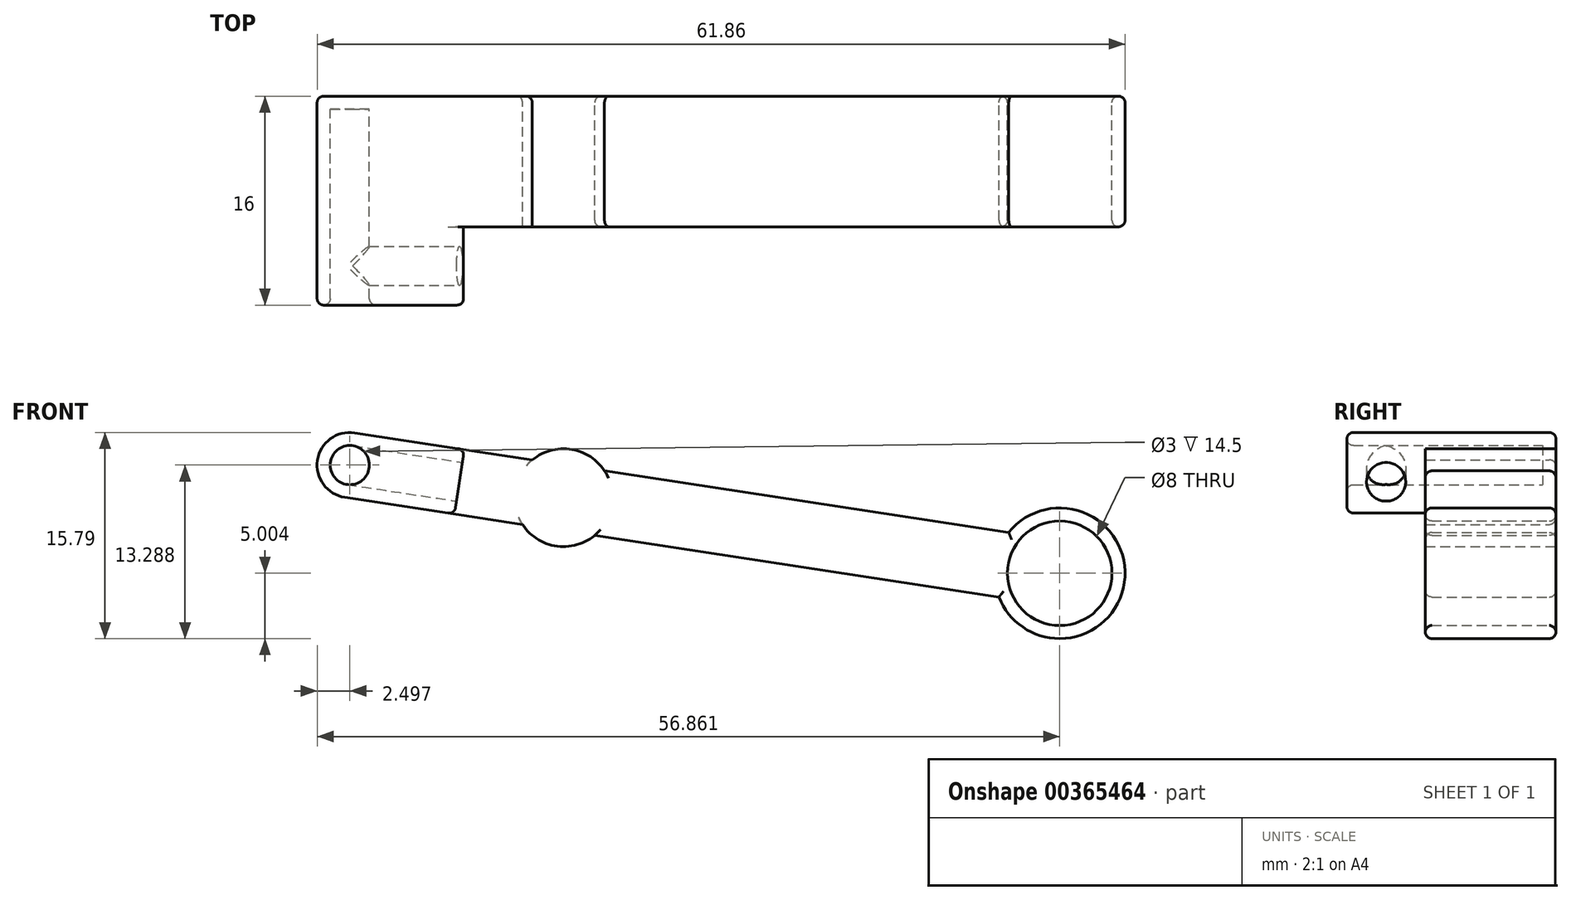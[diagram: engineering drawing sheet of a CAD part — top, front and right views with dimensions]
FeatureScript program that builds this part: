
annotation { "Feature Type Name" : "Feature", "Feature Type Description" : "" }
export const myFeature = defineFeature(function(context is Context, id is Id, definition is map)
    precondition{}
    {
        {
            var Q0;
            Q0=qCreatedBy(makeId("Front.planeOp"),FACE);
            var sketch = newSketch(context, id + "F0", { "sketchPlane" : qUnion([Q0])});
            skCircle(sketch, "E0", {"center": v(98.53, -16.59) * mm, "radius": 4 * mm});
            skCircle(sketch, "E1", {"center": v(44.17, -8.3) * mm, "radius": 1.5 * mm});
            skCircle(sketch, "E2", {"center": v(98.53, -16.59) * mm, "radius": 5 * mm});
            skCircle(sketch, "E3", {"center": v(44.17, -8.3) * mm, "radius": 2.5 * mm});
            skLineSegment(sketch, "E4", {"start": v(44.54, -5.83) * mm, "end": v(94.63, -13.46) * mm});
            skLineSegment(sketch, "E5.MirrorCS", {"start": v(43.8, -10.77) * mm, "end": v(93.87, -18.4) * mm});
            skCircle(sketch, "E6", {"center": v(60.53, -10.8) * mm, "radius": 3.75 * mm});
            skSolve(sketch);
        }
        {
            var Q0;
            Q0 = qSketchRegion(id + "F0", true);
            extrude(context, id + "F1", {"entities" : qUnion([Q0]), "depth" : 10 * mm});
        }
        {
            var Q0;
            Q0=makeQuery(id+"F1.opExtrude","CAP_FACE",FACE,{"disambiguationData":[OSD([sQuery(id+"F0.wireOp",EDGE,"E0"),sQuery(id+"F0.wireOp",EDGE,"E1"),sQuery(id+"F0.wireOp",EDGE,"E2"),sQuery(id+"F0.wireOp",EDGE,"E3"),sQuery(id+"F0.wireOp",EDGE,"E4"),sQuery(id+"F0.wireOp",EDGE,"E5.MirrorCS"),sQuery(id+"F0.wireOp",EDGE,"E6")])],"isStart":false});
            var sketch = newSketch(context, id + "F2", { "sketchPlane" : qUnion([Q0])});
            skCircle(sketch, "E7", {"center": v(44.17, -8.3) * mm, "radius": 1.5 * mm});
            skArc(sketch, "E8", {"start": v(44.54, -5.83) * mm, "mid": v(41.7, -7.93) * mm, "end": v(43.8, -10.77) * mm});
            skLineSegment(sketch, "E9", {"start": v(44.17, -8.3) * mm, "end": v(52.57, -9.58) * mm});
            skLineSegment(sketch, "E10", {"start": v(52.57, -9.58) * mm, "end": v(52.95, -7.11) * mm});
            skLineSegment(sketch, "E11", {"start": v(52.95, -7.11) * mm, "end": v(44.54, -5.83) * mm});
            skLineSegment(sketch, "E12", {"start": v(52.57, -9.58) * mm, "end": v(52.2, -12.05) * mm});
            skLineSegment(sketch, "E13", {"start": v(43.8, -10.77) * mm, "end": v(52.2, -12.05) * mm});
            skSolve(sketch);
        }
        {
            var Q0;
            Q0 = qSketchRegion(id + "F2", true);
            extrude(context, id + "F3", {"entities" : qUnion([Q0]), "operationType" : NewBodyOperationType.ADD, "depth" : 6 * mm});
        }
        {
            var Q0;
            Q0=makeQuery(id+"F3.opExtrude","CAP_EDGE",EDGE,{"disambiguationData":[OSD([sQuery(id+"F2.wireOp",EDGE,"E10"),sQuery(id+"F2.wireOp",EDGE,"E12")])],"isStart":false});
            var Q1;
            Q1=makeQuery(id+"F3.opExtrude","SWEPT_EDGE",EDGE,{"disambiguationData":[OSD([sQuery(id+"F0.wireOp",EDGE,"E4"),sQuery(id+"F2.wireOp",EDGE,"E10"),sQuery(id+"F2.wireOp",EDGE,"E11")])]});
            var Q2;
            Q2=makeQuery(id+"F3.opExtrude","CAP_EDGE",EDGE,{"disambiguationData":[OSD([sQuery(id+"F2.wireOp",EDGE,"E10"),sQuery(id+"F2.wireOp",EDGE,"E12")])],"isStart":true});
            var Q3;
            Q3=makeQuery(id+"F3.opExtrude","SWEPT_EDGE",EDGE,{"disambiguationData":[OSD([sQuery(id+"F0.wireOp",EDGE,"E5.MirrorCS"),sQuery(id+"F2.wireOp",EDGE,"E12"),sQuery(id+"F2.wireOp",EDGE,"E13")])]});
            var Q4;
            {var subQ0=sQuery(id+"F0.wireOp",EDGE,"E6");var subQ1=sQuery(id+"F0.wireOp",EDGE,"E4");Q4=makeQuery(id+"F1.opExtrude","CAP_EDGE",EDGE,{"disambiguationData":[OSD([subQ0]),TDD([makeQuery(id+"F0.imprint","IMPRINT",EDGE,{"disambiguationData":[TD([[makeQuery(id+"F0.imprint","INTERSECT",VERTEX,{"disambiguationData":[OD(0.0)],"derivedFrom":[subQ1,subQ0]}),1.0]])],"derivedFrom":subQ0})])],"isStart":false});}
            var Q5;
            {var subQ0=sQuery(id+"F0.wireOp",EDGE,"E6");var subQ1=sQuery(id+"F0.wireOp",EDGE,"E5.MirrorCS");Q5=makeQuery(id+"F1.opExtrude","CAP_EDGE",EDGE,{"disambiguationData":[OSD([subQ0]),TDD([makeQuery(id+"F0.imprint","IMPRINT",EDGE,{"disambiguationData":[TD([[makeQuery(id+"F0.imprint","INTERSECT",VERTEX,{"disambiguationData":[OD(0.0)],"derivedFrom":[subQ1,subQ0]}),-1.0]])],"derivedFrom":subQ0})])],"isStart":false});}
            var Q6;
            {var subQ0=sQuery(id+"F0.wireOp",EDGE,"E5.MirrorCS");Q6=makeQuery(id+"F1.opExtrude","CAP_EDGE",EDGE,{"disambiguationData":[OSD([subQ0]),TDD([makeQuery(id+"F0.imprint","IMPRINT",EDGE,{"disambiguationData":[TD([[makeQuery(id+"F0.imprint","INTERSECT",VERTEX,{"derivedFrom":[sQuery(id+"F0.wireOp",EDGE,"E2"),subQ0]}),1.0]])],"derivedFrom":subQ0})])],"isStart":false});}
            var Q7;
            {var subQ0=sQuery(id+"F0.wireOp",EDGE,"E4");Q7=makeQuery(id+"F1.opExtrude","CAP_EDGE",EDGE,{"disambiguationData":[OSD([subQ0]),TDD([makeQuery(id+"F0.imprint","IMPRINT",EDGE,{"disambiguationData":[TD([[makeQuery(id+"F0.imprint","INTERSECT",VERTEX,{"derivedFrom":[sQuery(id+"F0.wireOp",EDGE,"E2"),subQ0]}),1.0]])],"derivedFrom":subQ0})])],"isStart":false});}
            var Q8;
            Q8=makeQuery(id+"F1.opExtrude","CAP_EDGE",EDGE,{"disambiguationData":[OSD([sQuery(id+"F0.wireOp",EDGE,"E0")])],"isStart":false});
            var Q9;
            Q9=makeQuery(id+"F1.opExtrude","CAP_EDGE",EDGE,{"disambiguationData":[OSD([sQuery(id+"F0.wireOp",EDGE,"E2")])],"isStart":false});
            var Q10;
            Q10=makeQuery(id+"F1.opExtrude","CAP_EDGE",EDGE,{"disambiguationData":[OSD([sQuery(id+"F0.wireOp",EDGE,"E2")])],"isStart":true});
            var Q11;
            Q11=makeQuery(id+"F1.opExtrude","CAP_EDGE",EDGE,{"disambiguationData":[OSD([sQuery(id+"F0.wireOp",EDGE,"E0")])],"isStart":true});
            var Q12;
            {var subQ0=sQuery(id+"F0.wireOp",EDGE,"E4");Q12=makeQuery(id+"F1.opExtrude","CAP_EDGE",EDGE,{"disambiguationData":[OSD([subQ0]),TDD([makeQuery(id+"F0.imprint","IMPRINT",EDGE,{"disambiguationData":[TD([[makeQuery(id+"F0.imprint","INTERSECT",VERTEX,{"derivedFrom":[sQuery(id+"F0.wireOp",EDGE,"E2"),subQ0]}),1.0]])],"derivedFrom":subQ0})])],"isStart":true});}
            var Q13;
            {var subQ0=sQuery(id+"F0.wireOp",EDGE,"E5.MirrorCS");Q13=makeQuery(id+"F1.opExtrude","CAP_EDGE",EDGE,{"disambiguationData":[OSD([subQ0]),TDD([makeQuery(id+"F0.imprint","IMPRINT",EDGE,{"disambiguationData":[TD([[makeQuery(id+"F0.imprint","INTERSECT",VERTEX,{"derivedFrom":[sQuery(id+"F0.wireOp",EDGE,"E2"),subQ0]}),1.0]])],"derivedFrom":subQ0})])],"isStart":true});}
            var Q14;
            {var subQ0=sQuery(id+"F0.wireOp",EDGE,"E6");var subQ1=sQuery(id+"F0.wireOp",EDGE,"E4");Q14=makeQuery(id+"F1.opExtrude","CAP_EDGE",EDGE,{"disambiguationData":[OSD([subQ0]),TDD([makeQuery(id+"F0.imprint","IMPRINT",EDGE,{"disambiguationData":[TD([[makeQuery(id+"F0.imprint","INTERSECT",VERTEX,{"disambiguationData":[OD(0.0)],"derivedFrom":[subQ1,subQ0]}),1.0]])],"derivedFrom":subQ0})])],"isStart":true});}
            var Q15;
            {var subQ0=sQuery(id+"F0.wireOp",EDGE,"E6");var subQ1=sQuery(id+"F0.wireOp",EDGE,"E5.MirrorCS");Q15=makeQuery(id+"F1.opExtrude","CAP_EDGE",EDGE,{"disambiguationData":[OSD([subQ0]),TDD([makeQuery(id+"F0.imprint","IMPRINT",EDGE,{"disambiguationData":[TD([[makeQuery(id+"F0.imprint","INTERSECT",VERTEX,{"disambiguationData":[OD(0.0)],"derivedFrom":[subQ1,subQ0]}),-1.0]])],"derivedFrom":subQ0})])],"isStart":true});}
            var Q16;
            {var subQ0=sQuery(id+"F0.wireOp",EDGE,"E5.MirrorCS");Q16=makeQuery(id+"F1.opExtrude","CAP_EDGE",EDGE,{"disambiguationData":[OSD([subQ0]),TDD([makeQuery(id+"F0.imprint","IMPRINT",EDGE,{"disambiguationData":[TD([[makeQuery(id+"F0.imprint","INTERSECT",VERTEX,{"derivedFrom":[sQuery(id+"F0.wireOp",EDGE,"E3"),subQ0]}),-1.0]])],"derivedFrom":subQ0})])],"isStart":true});}
            var Q17;
            Q17=makeQuery(id+"F3.opExtrude","CAP_EDGE",EDGE,{"disambiguationData":[OSD([sQuery(id+"F2.wireOp",EDGE,"E8")])],"isStart":false});
            var Q18;
            Q18=makeQuery(id+"F3.opExtrude","CAP_EDGE",EDGE,{"disambiguationData":[OSD([sQuery(id+"F2.wireOp",EDGE,"E7")])],"isStart":false});
            fillet(context, id + "F4", {"entities" : qUnion([Q0, Q1, Q2, Q3, Q4, Q5, Q6, Q7, Q8, Q9, Q10, Q11, Q12, Q13, Q14, Q15, Q16, Q17, Q18]), "radius" : 0.5 * mm, "tangentPropagation" : true, "allowEdgeOverflow" : false});
        }
        {
            var Q0;
            Q0=makeQuery(id+"F1.opExtrude","CAP_FACE",FACE,{"disambiguationData":[OSD([sQuery(id+"F0.wireOp",EDGE,"E0"),sQuery(id+"F0.wireOp",EDGE,"E1"),sQuery(id+"F0.wireOp",EDGE,"E2"),sQuery(id+"F0.wireOp",EDGE,"E3"),sQuery(id+"F0.wireOp",EDGE,"E4"),sQuery(id+"F0.wireOp",EDGE,"E5.MirrorCS"),sQuery(id+"F0.wireOp",EDGE,"E6")])],"isStart":true});
            var sketch = newSketch(context, id + "F5", { "sketchPlane" : qUnion([Q0])});
            skCircle(sketch, "E14", {"center": v(-44.17, -8.3) * mm, "radius": 1.75 * mm});
            skSolve(sketch);
        }
        {
            var Q0;
            Q0 = qSketchRegion(id + "F5", true);
            extrude(context, id + "F6", {"entities" : qUnion([Q0]), "operationType" : NewBodyOperationType.ADD, "oppositeDirection" : true, "depth" : 1 * mm});
        }
        {
            var Q0;
            Q0=makeQuery(id+"F3.opExtrude","SWEPT_FACE",FACE,{"disambiguationData":[OSD([sQuery(id+"F2.wireOp",EDGE,"E10"),sQuery(id+"F2.wireOp",EDGE,"E12")])]});
            var sketch = newSketch(context, id + "F7", { "sketchPlane" : qUnion([Q0])});
            skCircle(sketch, "E15", {"center": v(-13, -1.55) * mm, "radius": 1.5 * mm});
            skPoint(sketch, "E15.centerSnap0", {"position": v(-15.5, -1.55) * mm});
            skPoint(sketch, "E15.centerSnap1", {"position": v(-13, 0.45) * mm});
            skSolve(sketch);
        }
        {
            var Q0;
            Q0 = qSketchRegion(id + "F7", true);
            extrude(context, id + "F8", {"entities" : qUnion([Q0]), "operationType" : NewBodyOperationType.REMOVE, "oppositeDirection" : true, "depth" : 8.5 * mm});
        }
    });
